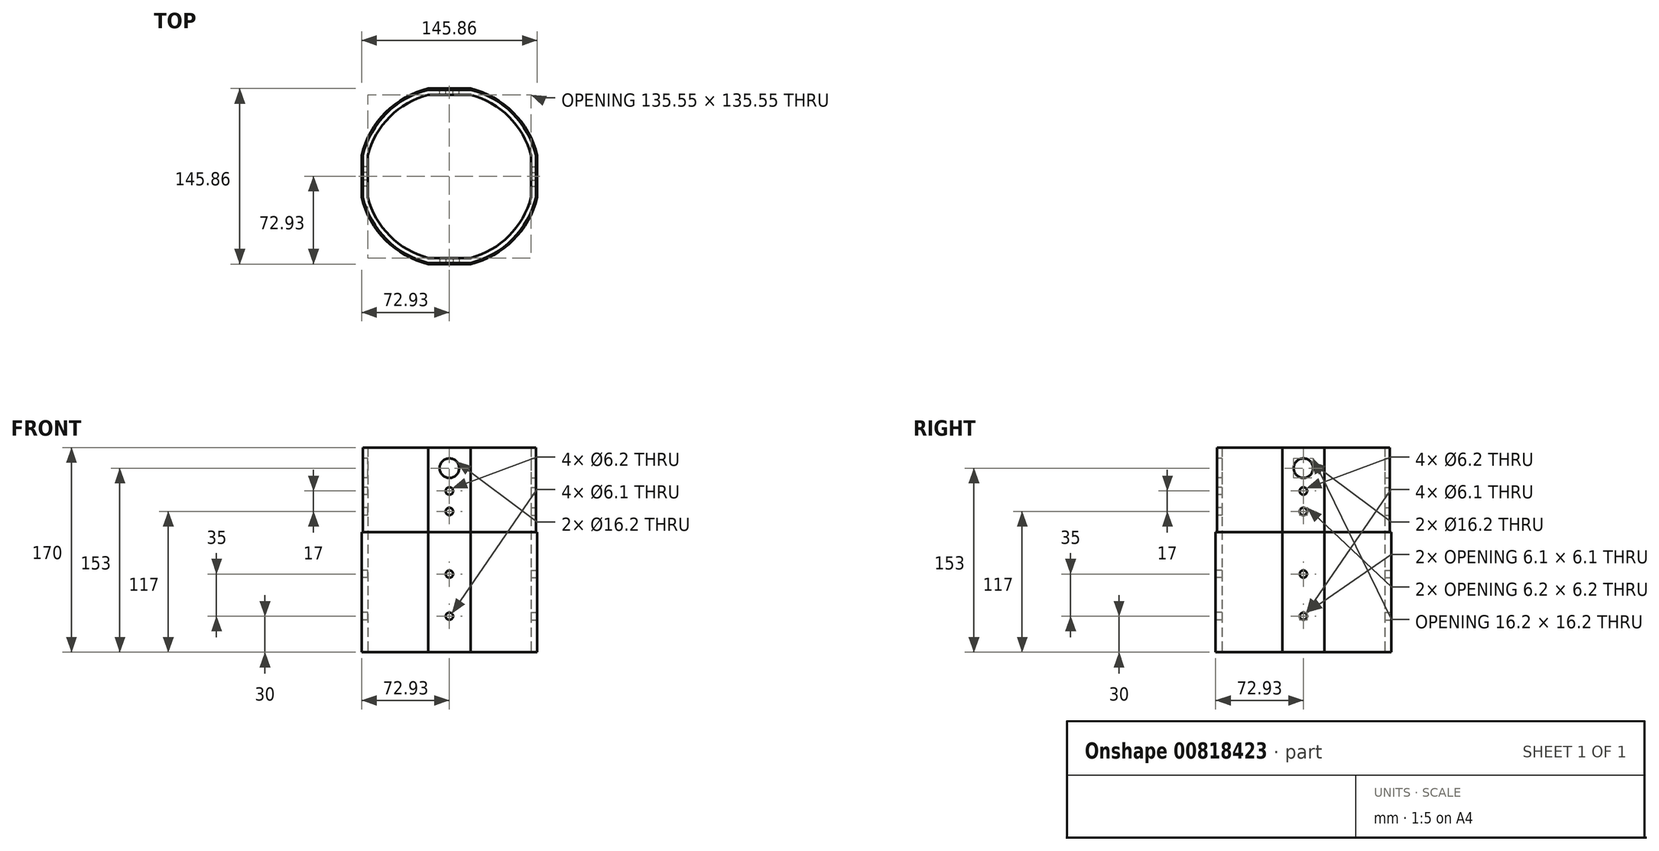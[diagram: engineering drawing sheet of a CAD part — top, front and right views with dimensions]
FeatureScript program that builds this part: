
annotation { "Feature Type Name" : "Feature", "Feature Type Description" : "" }
export const myFeature = defineFeature(function(context is Context, id is Id, definition is map)
    precondition{}
    {
        {
            var Q0;
            Q0=qCreatedBy(makeId("Top.planeOp"),FACE);
            var sketch = newSketch(context, id + "F0", { "sketchPlane" : qUnion([Q0])});
            skArc(sketch, "E0", {"start": v(-17.5, 72.93) * mm, "mid": v(-53.03, 53.03) * mm, "end": v(-72.93, 17.5) * mm});
            skArc(sketch, "E1", {"start": v(-72.93, -17.5) * mm, "mid": v(-53.03, -53.03) * mm, "end": v(-17.5, -72.93) * mm});
            skArc(sketch, "E2", {"start": v(17.5, -72.93) * mm, "mid": v(53.03, -53.03) * mm, "end": v(72.93, -17.5) * mm});
            skArc(sketch, "E3", {"start": v(72.93, 17.5) * mm, "mid": v(53.03, 53.03) * mm, "end": v(17.5, 72.93) * mm});
            skLineSegment(sketch, "E4", {"start": v(-72.93, 17.5) * mm, "end": v(-72.93, -17.5) * mm});
            skLineSegment(sketch, "E5", {"start": v(-17.5, 72.93) * mm, "end": v(17.5, 72.93) * mm});
            skLineSegment(sketch, "E6", {"start": v(72.93, 17.5) * mm, "end": v(72.93, -17.5) * mm});
            skLineSegment(sketch, "E7", {"start": v(-17.5, -72.93) * mm, "end": v(17.5, -72.93) * mm});
            skArc(sketch, "E8", {"start": v(-17.5, 67.78) * mm, "mid": v(-49.5, 49.5) * mm, "end": v(-67.78, 17.5) * mm});
            skArc(sketch, "E9", {"start": v(-67.78, -17.5) * mm, "mid": v(-49.5, -49.5) * mm, "end": v(-17.5, -67.78) * mm});
            skArc(sketch, "E10", {"start": v(17.5, -67.78) * mm, "mid": v(49.5, -49.5) * mm, "end": v(67.78, -17.5) * mm});
            skArc(sketch, "E11", {"start": v(67.78, 17.5) * mm, "mid": v(49.5, 49.5) * mm, "end": v(17.5, 67.78) * mm});
            skLineSegment(sketch, "E12", {"start": v(-17.5, 67.78) * mm, "end": v(17.5, 67.78) * mm});
            skLineSegment(sketch, "E13", {"start": v(-67.78, 17.5) * mm, "end": v(-67.78, -17.5) * mm});
            skLineSegment(sketch, "E14", {"start": v(-17.5, -67.78) * mm, "end": v(17.5, -67.78) * mm});
            skLineSegment(sketch, "E15", {"start": v(67.78, -17.5) * mm, "end": v(67.78, 17.5) * mm});
            skSolve(sketch);
        }
        {
            var Q0;
            Q0=qSketchRegion(id+"F0",true);
            extrude(context, id + "F1", {"entities" : qUnion([Q0]), "depth" : 100 * mm, "offsetDistance" : 25 * mm});
        }
        {
            var Q0;
            Q0=makeQuery(id+"F1.opExtrude","CAP_FACE",FACE,{"disambiguationData":[OSD([sQuery(id+"F0.wireOp",EDGE,"E0"),sQuery(id+"F0.wireOp",EDGE,"E1"),sQuery(id+"F0.wireOp",EDGE,"E2"),sQuery(id+"F0.wireOp",EDGE,"E3"),sQuery(id+"F0.wireOp",EDGE,"E4"),sQuery(id+"F0.wireOp",EDGE,"E5"),sQuery(id+"F0.wireOp",EDGE,"E6"),sQuery(id+"F0.wireOp",EDGE,"E7"),sQuery(id+"F0.wireOp",EDGE,"E8"),sQuery(id+"F0.wireOp",EDGE,"E9"),sQuery(id+"F0.wireOp",EDGE,"E10"),sQuery(id+"F0.wireOp",EDGE,"E11"),sQuery(id+"F0.wireOp",EDGE,"E12"),sQuery(id+"F0.wireOp",EDGE,"E13"),sQuery(id+"F0.wireOp",EDGE,"E14"),sQuery(id+"F0.wireOp",EDGE,"E15")])],"isStart":false});
            var sketch = newSketch(context, id + "F2", { "sketchPlane" : qUnion([Q0])});
            skArc(sketch, "E16.0", {"start": v(-17.5, 67.78) * mm, "mid": v(-49.5, 49.5) * mm, "end": v(-67.78, 17.5) * mm});
            skLineSegment(sketch, "E16.1", {"start": v(-67.78, 17.5) * mm, "end": v(-67.78, -17.5) * mm});
            skArc(sketch, "E16.2", {"start": v(-67.78, -17.5) * mm, "mid": v(-49.5, -49.5) * mm, "end": v(-17.5, -67.78) * mm});
            skLineSegment(sketch, "E16.3", {"start": v(-17.5, -67.78) * mm, "end": v(17.5, -67.78) * mm});
            skArc(sketch, "E16.4", {"start": v(17.5, -67.78) * mm, "mid": v(49.5, -49.5) * mm, "end": v(67.78, -17.5) * mm});
            skLineSegment(sketch, "E16.5", {"start": v(67.78, -17.5) * mm, "end": v(67.78, 17.5) * mm});
            skArc(sketch, "E16.6", {"start": v(67.78, 17.5) * mm, "mid": v(49.5, 49.5) * mm, "end": v(17.5, 67.78) * mm});
            skLineSegment(sketch, "E16.7", {"start": v(-17.5, 67.78) * mm, "end": v(17.5, 67.78) * mm});
            skArc(sketch, "E17", {"start": v(-17.5, 71.9) * mm, "mid": v(-52.33, 52.33) * mm, "end": v(-71.9, 17.5) * mm});
            skArc(sketch, "E18", {"start": v(71.9, 17.5) * mm, "mid": v(52.33, 52.33) * mm, "end": v(17.5, 71.9) * mm});
            skLineSegment(sketch, "E19", {"start": v(-71.9, 17.5) * mm, "end": v(-71.9, -17.5) * mm});
            skLineSegment(sketch, "E20", {"start": v(-17.5, 71.9) * mm, "end": v(17.5, 71.9) * mm});
            skPoint(sketch, "E21.start.orphan", {"position": v(26, -67.78) * mm});
            skLineSegment(sketch, "E22", {"start": v(71.9, 17.5) * mm, "end": v(71.9, -17.5) * mm});
            skArc(sketch, "E23", {"start": v(-71.9, -17.5) * mm, "mid": v(-52.33, -52.33) * mm, "end": v(-17.5, -71.9) * mm});
            skArc(sketch, "E24", {"start": v(71.9, -17.5) * mm, "mid": v(52.33, -52.33) * mm, "end": v(17.5, -71.9) * mm});
            skLineSegment(sketch, "E25", {"start": v(-17.5, -71.9) * mm, "end": v(17.5, -71.9) * mm});
            skSolve(sketch);
        }
        {
            var Q0;
            Q0=qSketchRegion(id+"F2",true);
            extrude(context, id + "F3", {"entities" : qUnion([Q0]), "operationType" : NewBodyOperationType.ADD, "depth" : 70 * mm, "offsetDistance" : 25 * mm});
        }
        {
            var Q0;
            Q0=makeQuery(id+"F3.opExtrude","SWEPT_FACE",FACE,{"disambiguationData":[OSD([sQuery(id+"F2.wireOp",EDGE,"E25")])]});
            var sketch = newSketch(context, id + "F4", { "sketchPlane" : qUnion([Q0])});
            skCircle(sketch, "E26", {"center": v(0, 153) * mm, "radius": 8.1 * mm});
            skCircle(sketch, "E27", {"center": v(0, 134) * mm, "radius": 3.1 * mm});
            skCircle(sketch, "E28", {"center": v(0, 117) * mm, "radius": 3.1 * mm});
            skSolve(sketch);
        }
        {
            var Q0;
            Q0=qSketchRegion(id+"F4",true);
            var Q1;
            Q1=makeQuery(id+"F3.boolean.opBoolean","MERGE",FACE,{"derivedFrom":[makeQuery(id+"F1.opExtrude","SWEPT_FACE",FACE,{"disambiguationData":[OSD([sQuery(id+"F0.wireOp",EDGE,"E14")])]}),makeQuery(id+"F3.opExtrude","SWEPT_FACE",FACE,{"disambiguationData":[OSD([sQuery(id+"F2.wireOp",EDGE,"E16.3")])]})]});
            extrude(context, id + "F5", {"entities" : qUnion([Q0]), "operationType" : NewBodyOperationType.REMOVE, "endBound" : BoundingType.UP_TO_SURFACE, "oppositeDirection" : true, "depth" : 25 * mm, "endBoundEntityFace" : qUnion([Q1]), "offsetDistance" : 25 * mm});
        }
        {
            var Q0;
            Q0=makeQuery(id+"F3.opExtrude","SWEPT_FACE",FACE,{"disambiguationData":[OSD([sQuery(id+"F2.wireOp",EDGE,"E22")])]});
            var sketch = newSketch(context, id + "F6", { "sketchPlane" : qUnion([Q0])});
            skCircle(sketch, "E29", {"center": v(0, 153) * mm, "radius": 8.1 * mm});
            skCircle(sketch, "E30", {"center": v(0, 134) * mm, "radius": 3.1 * mm});
            skCircle(sketch, "E31", {"center": v(0, 117) * mm, "radius": 3.1 * mm});
            skSolve(sketch);
        }
        {
            var Q0;
            Q0=qSketchRegion(id+"F6",true);
            var Q1;
            Q1=makeQuery(id+"F3.boolean.opBoolean","MERGE",FACE,{"derivedFrom":[makeQuery(id+"F1.opExtrude","SWEPT_FACE",FACE,{"disambiguationData":[OSD([sQuery(id+"F0.wireOp",EDGE,"E15")])]}),makeQuery(id+"F3.opExtrude","SWEPT_FACE",FACE,{"disambiguationData":[OSD([sQuery(id+"F2.wireOp",EDGE,"E16.5")])]})]});
            extrude(context, id + "F7", {"entities" : qUnion([Q0]), "operationType" : NewBodyOperationType.REMOVE, "endBound" : BoundingType.UP_TO_SURFACE, "oppositeDirection" : true, "depth" : 25 * mm, "endBoundEntityFace" : qUnion([Q1]), "offsetDistance" : 25 * mm});
        }
        {
            var Q0;
            Q0=makeQuery(id+"F3.opExtrude","SWEPT_FACE",FACE,{"disambiguationData":[OSD([sQuery(id+"F2.wireOp",EDGE,"E20")])]});
            var sketch = newSketch(context, id + "F8", { "sketchPlane" : qUnion([Q0])});
            skCircle(sketch, "E32", {"center": v(0, 153) * mm, "radius": 8.1 * mm});
            skCircle(sketch, "E33", {"center": v(0, 134) * mm, "radius": 3.1 * mm});
            skCircle(sketch, "E34", {"center": v(0, 117) * mm, "radius": 3.1 * mm});
            skSolve(sketch);
        }
        {
            var Q0;
            Q0=qSketchRegion(id+"F8",true);
            var Q1;
            Q1=makeQuery(id+"F3.boolean.opBoolean","MERGE",FACE,{"derivedFrom":[makeQuery(id+"F1.opExtrude","SWEPT_FACE",FACE,{"disambiguationData":[OSD([sQuery(id+"F0.wireOp",EDGE,"E12")])]}),makeQuery(id+"F3.opExtrude","SWEPT_FACE",FACE,{"disambiguationData":[OSD([sQuery(id+"F2.wireOp",EDGE,"E16.7")])]})]});
            extrude(context, id + "F9", {"entities" : qUnion([Q0]), "operationType" : NewBodyOperationType.REMOVE, "endBound" : BoundingType.UP_TO_SURFACE, "oppositeDirection" : true, "depth" : 25 * mm, "endBoundEntityFace" : qUnion([Q1]), "offsetDistance" : 25 * mm});
        }
        {
            var Q0;
            Q0=makeQuery(id+"F3.opExtrude","SWEPT_FACE",FACE,{"disambiguationData":[OSD([sQuery(id+"F2.wireOp",EDGE,"E19")])]});
            var sketch = newSketch(context, id + "F10", { "sketchPlane" : qUnion([Q0])});
            skCircle(sketch, "E35", {"center": v(0, 153) * mm, "radius": 8.1 * mm});
            skCircle(sketch, "E36", {"center": v(0, 134) * mm, "radius": 3.1 * mm});
            skCircle(sketch, "E37", {"center": v(0, 117) * mm, "radius": 3.1 * mm});
            skSolve(sketch);
        }
        {
            var Q0;
            Q0=qSketchRegion(id+"F10",true);
            extrude(context, id + "F11", {"entities" : qUnion([Q0]), "operationType" : NewBodyOperationType.REMOVE, "endBound" : BoundingType.UP_TO_NEXT, "oppositeDirection" : true, "depth" : 25 * mm, "offsetDistance" : 25 * mm});
        }
        {
            var Q0;
            Q0=makeQuery(id+"F1.opExtrude","SWEPT_FACE",FACE,{"disambiguationData":[OSD([sQuery(id+"F0.wireOp",EDGE,"E6")])]});
            var sketch = newSketch(context, id + "F12", { "sketchPlane" : qUnion([Q0])});
            skCircle(sketch, "E38", {"center": v(0, 65) * mm, "radius": 3.05 * mm});
            skCircle(sketch, "E39", {"center": v(0, 30) * mm, "radius": 3.05 * mm});
            skSolve(sketch);
        }
        {
            var Q0;
            Q0=qSketchRegion(id+"F12",true);
            extrude(context, id + "F13", {"entities" : qUnion([Q0]), "operationType" : NewBodyOperationType.REMOVE, "endBound" : BoundingType.UP_TO_NEXT, "oppositeDirection" : true, "depth" : 25 * mm, "offsetDistance" : 25 * mm});
        }
        {
            var Q0;
            Q0=makeQuery(id+"F1.opExtrude","SWEPT_FACE",FACE,{"disambiguationData":[OSD([sQuery(id+"F0.wireOp",EDGE,"E7")])]});
            var sketch = newSketch(context, id + "F14", { "sketchPlane" : qUnion([Q0])});
            skCircle(sketch, "E40", {"center": v(0, 65) * mm, "radius": 3.05 * mm});
            skCircle(sketch, "E41", {"center": v(0, 30) * mm, "radius": 3.05 * mm});
            skSolve(sketch);
        }
        {
            var Q0;
            Q0=qSketchRegion(id+"F14",true);
            extrude(context, id + "F15", {"entities" : qUnion([Q0]), "operationType" : NewBodyOperationType.REMOVE, "endBound" : BoundingType.UP_TO_NEXT, "oppositeDirection" : true, "depth" : 25 * mm, "offsetDistance" : 25 * mm});
        }
        {
            var Q0;
            Q0=makeQuery(id+"F1.opExtrude","SWEPT_FACE",FACE,{"disambiguationData":[OSD([sQuery(id+"F0.wireOp",EDGE,"E5")])]});
            var sketch = newSketch(context, id + "F16", { "sketchPlane" : qUnion([Q0])});
            skCircle(sketch, "E42", {"center": v(0, 65) * mm, "radius": 3.05 * mm});
            skCircle(sketch, "E43", {"center": v(0, 30) * mm, "radius": 3.05 * mm});
            skSolve(sketch);
        }
        {
            var Q0;
            Q0=qSketchRegion(id+"F16",true);
            extrude(context, id + "F17", {"entities" : qUnion([Q0]), "operationType" : NewBodyOperationType.REMOVE, "endBound" : BoundingType.UP_TO_NEXT, "oppositeDirection" : true, "depth" : 25 * mm, "offsetDistance" : 25 * mm});
        }
        {
            var Q0;
            Q0=makeQuery(id+"F1.opExtrude","SWEPT_FACE",FACE,{"disambiguationData":[OSD([sQuery(id+"F0.wireOp",EDGE,"E4")])]});
            var sketch = newSketch(context, id + "F18", { "sketchPlane" : qUnion([Q0])});
            skCircle(sketch, "E44", {"center": v(0, 65) * mm, "radius": 3.05 * mm});
            skCircle(sketch, "E45", {"center": v(0, 30) * mm, "radius": 3.05 * mm});
            skSolve(sketch);
        }
        {
            var Q0;
            Q0=qSketchRegion(id+"F18",true);
            extrude(context, id + "F19", {"entities" : qUnion([Q0]), "operationType" : NewBodyOperationType.REMOVE, "endBound" : BoundingType.UP_TO_NEXT, "oppositeDirection" : true, "depth" : 25 * mm, "offsetDistance" : 25 * mm});
        }
    });
